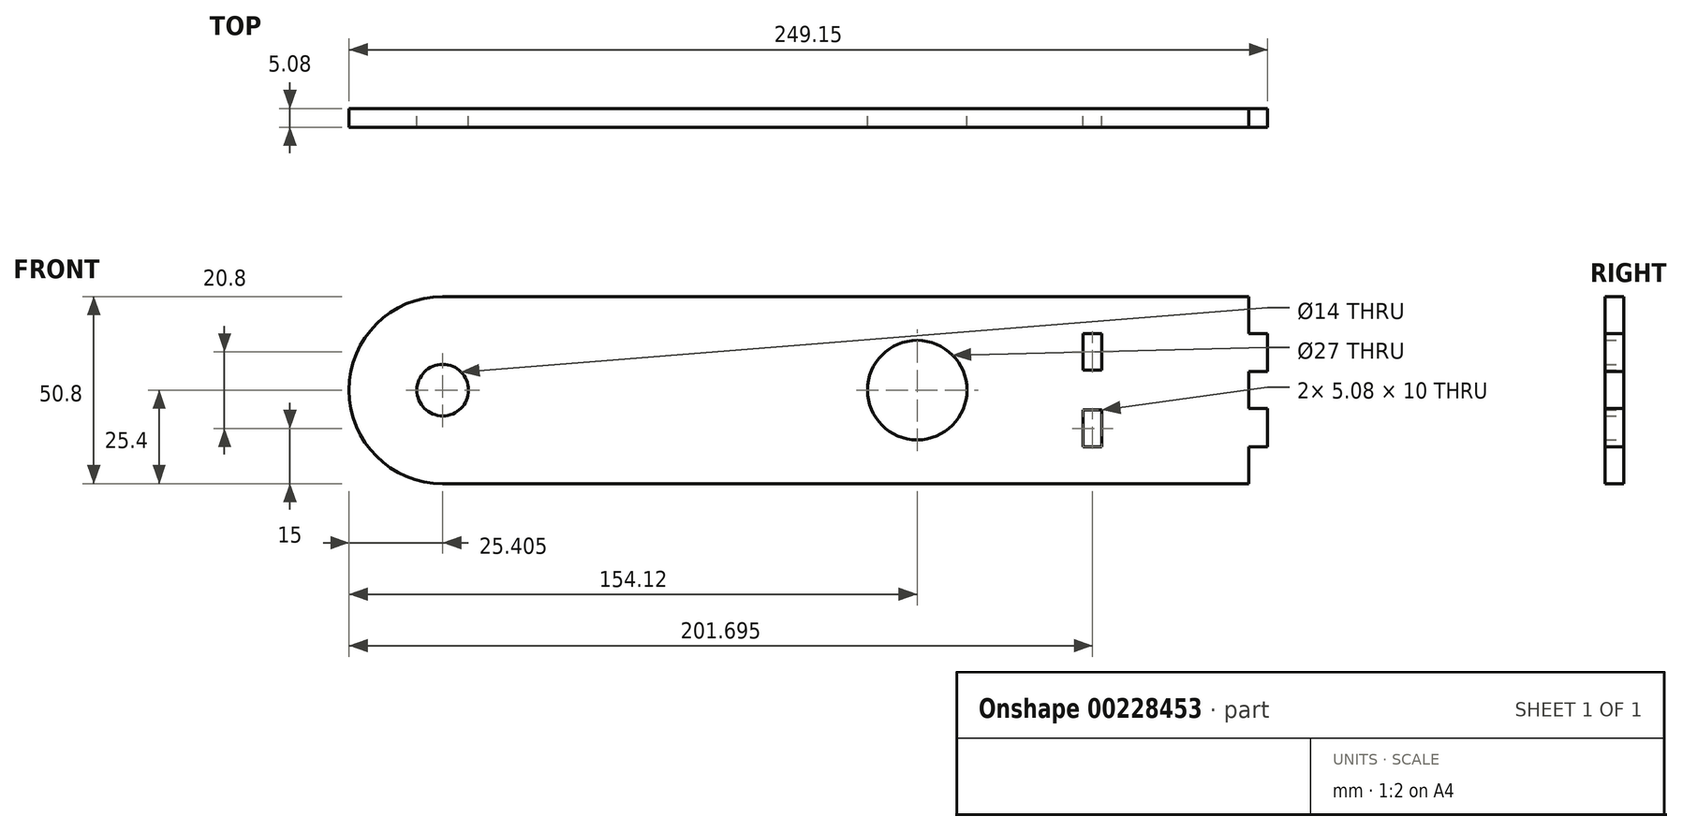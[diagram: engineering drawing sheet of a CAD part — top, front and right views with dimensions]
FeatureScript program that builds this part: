
annotation { "Feature Type Name" : "Feature", "Feature Type Description" : "" }
export const myFeature = defineFeature(function(context is Context, id is Id, definition is map)
    precondition{}
    {
        {
            var Q0;
            Q0=qCreatedBy(makeId("Front.planeOp"),FACE);
            var sketch = newSketch(context, id + "F0", { "sketchPlane" : qUnion([Q0])});
            skArc(sketch, "E0", {"start": v(-128.71, 25.4) * mm, "mid": v(-154.11, 0) * mm, "end": v(-128.71, -25.4) * mm});
            skLineSegment(sketch, "E1", {"start": v(0, 25.4) * mm, "end": v(-128.71, 25.4) * mm});
            skLineSegment(sketch, "E2", {"start": v(-128.71, -25.4) * mm, "end": v(0, -25.4) * mm});
            skCircle(sketch, "E3", {"center": v(-128.71, 0) * mm, "radius": 7 * mm});
            skCircle(sketch, "E4", {"center": v(0, 0) * mm, "radius": 13.5 * mm});
            skLineSegment(sketch, "E5", {"start": v(0, 25.4) * mm, "end": v(89.96, 25.4) * mm});
            skLineSegment(sketch, "E6", {"start": v(95.04, 15.4) * mm, "end": v(95.04, 5) * mm});
            skLineSegment(sketch, "E7", {"start": v(89.96, -25.4) * mm, "end": v(0, -25.4) * mm});
            skLineSegment(sketch, "E8", {"start": v(45.04, 25.4) * mm, "end": v(45.04, -25.4) * mm});
            skLineSegment(sketch, "E9.bottom", {"start": v(45.04, 15.4) * mm, "end": v(50.12, 15.4) * mm});
            skLineSegment(sketch, "E9.top", {"start": v(45.04, 5.4) * mm, "end": v(50.12, 5.4) * mm});
            skLineSegment(sketch, "E9.left", {"start": v(45.04, 15.4) * mm, "end": v(45.04, 5.4) * mm});
            skLineSegment(sketch, "E9.right", {"start": v(50.12, 15.4) * mm, "end": v(50.12, 5.4) * mm});
            skLineSegment(sketch, "E10", {"start": v(45.04, -15.4) * mm, "end": v(50.12, -15.4) * mm});
            skLineSegment(sketch, "E11", {"start": v(50.12, -15.4) * mm, "end": v(50.12, -5.4) * mm});
            skLineSegment(sketch, "E12", {"start": v(50.12, -5.4) * mm, "end": v(45.04, -5.4) * mm});
            skLineSegment(sketch, "E13.top", {"start": v(95.04, 15.4) * mm, "end": v(89.96, 15.4) * mm});
            skLineSegment(sketch, "E13.right", {"start": v(89.96, 25.4) * mm, "end": v(89.96, 15.4) * mm});
            skLineSegment(sketch, "E14.bottom", {"start": v(95.04, 5) * mm, "end": v(89.96, 5) * mm});
            skLineSegment(sketch, "E14.top", {"start": v(95.04, -5) * mm, "end": v(89.96, -5) * mm});
            skLineSegment(sketch, "E14.right", {"start": v(89.96, 5) * mm, "end": v(89.96, -5) * mm});
            skLineSegment(sketch, "E15.top", {"start": v(95.04, -15.4) * mm, "end": v(89.96, -15.4) * mm});
            skLineSegment(sketch, "E15.right", {"start": v(89.96, -25.4) * mm, "end": v(89.96, -15.4) * mm});
            skLineSegment(sketch, "E16.trimOffspring", {"start": v(95.04, -5) * mm, "end": v(95.04, -15.4) * mm});
            skSolve(sketch);
        }
        {
            var Q0;
            Q0 = qSketchRegion(id + "F0", true);
            extrude(context, id + "F1", {"entities" : qUnion([Q0]), "depth" : 5.08 * mm});
        }
    });
